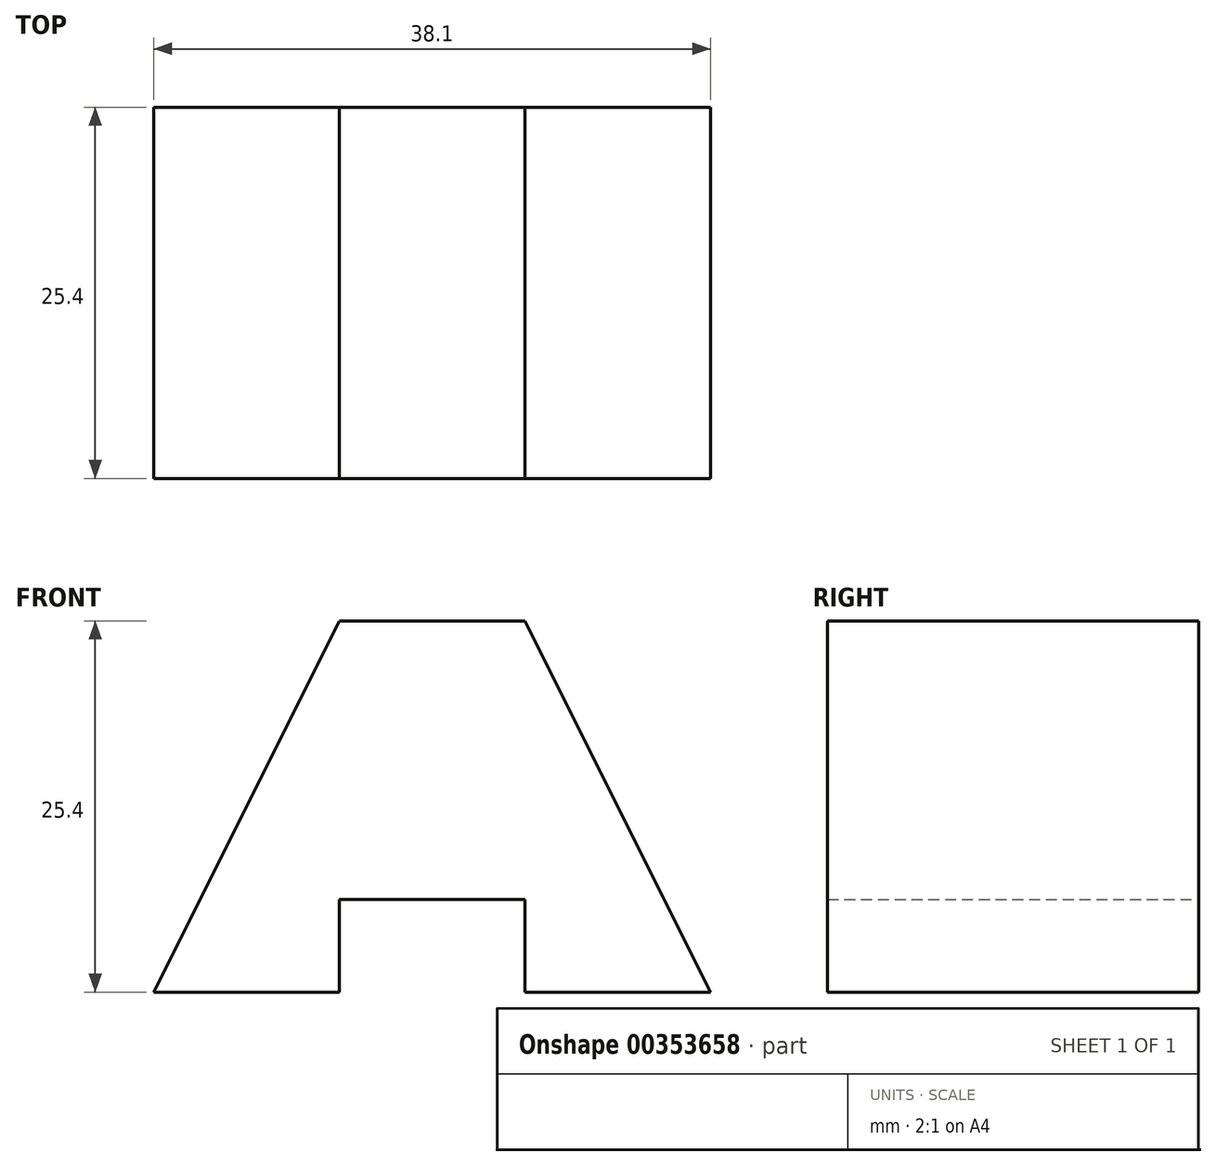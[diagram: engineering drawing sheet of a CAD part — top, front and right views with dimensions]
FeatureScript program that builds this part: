
annotation { "Feature Type Name" : "Feature", "Feature Type Description" : "" }
export const myFeature = defineFeature(function(context is Context, id is Id, definition is map)
    precondition{}
    {
        {
            var Q0;
            Q0=qCreatedBy(makeId("Front.planeOp"),FACE);
            var sketch = newSketch(context, id + "F0", { "sketchPlane" : qUnion([Q0])});
            skLineSegment(sketch, "E0", {"start": v(-25.4, 25.4) * mm, "end": v(-12.7, 25.4) * mm});
            skLineSegment(sketch, "E1", {"start": v(-12.7, 25.4) * mm, "end": v(0, 0) * mm});
            skLineSegment(sketch, "E2", {"start": v(0, 0) * mm, "end": v(-12.7, 0) * mm});
            skLineSegment(sketch, "E3", {"start": v(-12.7, 0) * mm, "end": v(-12.7, 6.35) * mm});
            skLineSegment(sketch, "E4", {"start": v(-12.7, 6.35) * mm, "end": v(-25.4, 6.35) * mm});
            skLineSegment(sketch, "E5", {"start": v(-25.4, 6.35) * mm, "end": v(-25.4, 0) * mm});
            skLineSegment(sketch, "E6", {"start": v(-25.4, 0) * mm, "end": v(-38.1, 0) * mm});
            skLineSegment(sketch, "E7", {"start": v(-38.1, 0) * mm, "end": v(-25.4, 25.4) * mm});
            skSolve(sketch);
        }
        {
            var Q0;
            Q0=makeQuery(id+"F0.imprint","IMPRINT",FACE,{"disambiguationData":[TD([[makeQuery(id+"F0.imprint","IMPRINT",EDGE,{"derivedFrom":sQuery(id+"F0.wireOp",EDGE,"E0")}),-1.0]])]});
            extrude(context, id + "F1", {"entities" : qUnion([Q0]), "depth" : 25.4 * mm});
        }
    });
